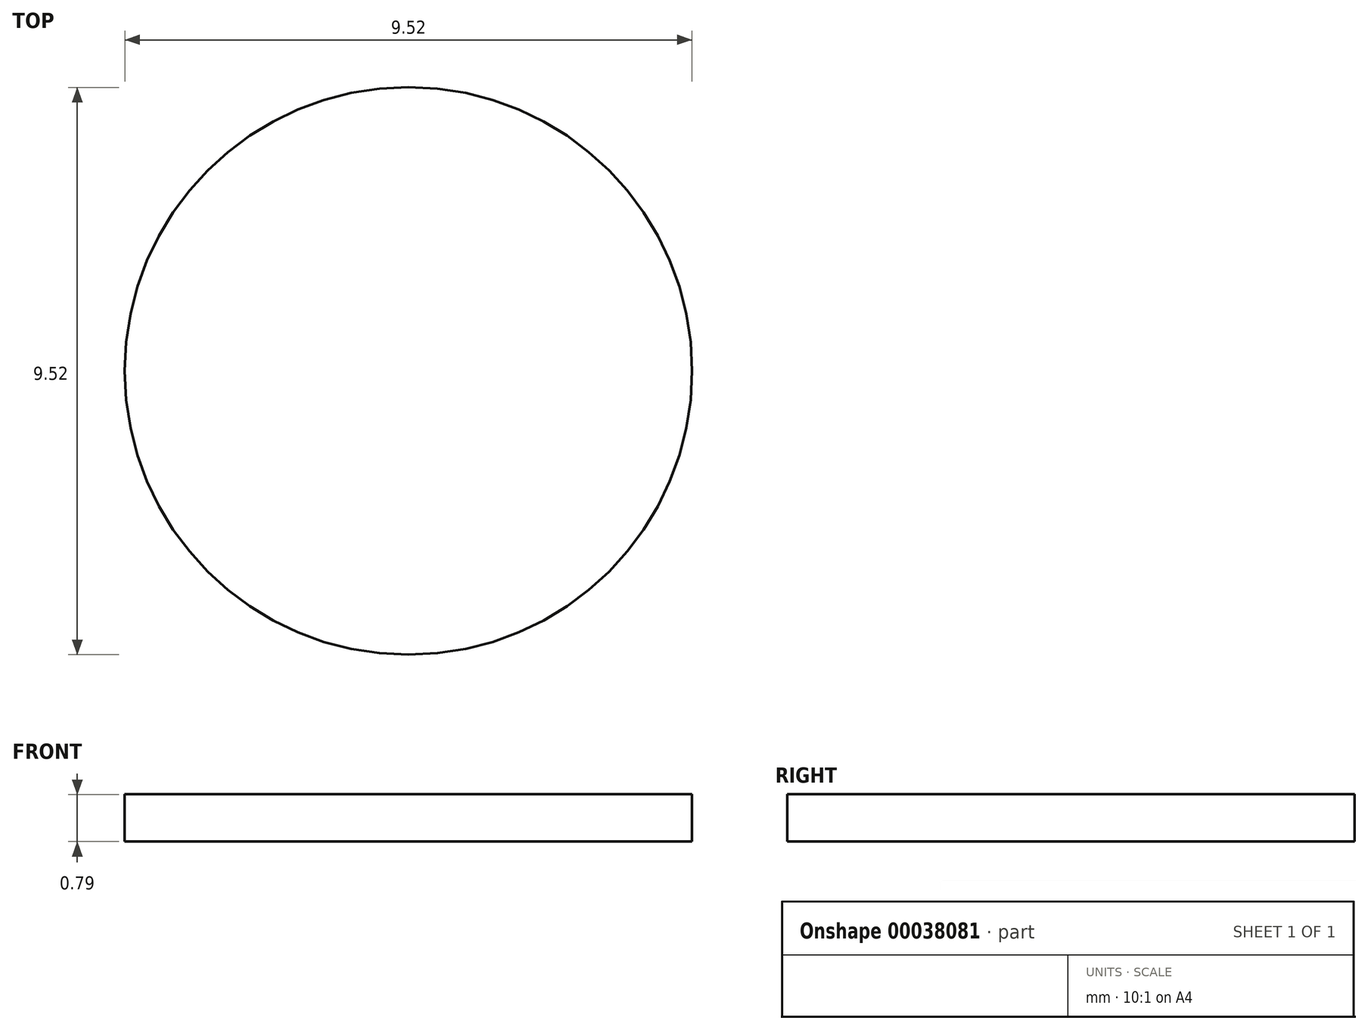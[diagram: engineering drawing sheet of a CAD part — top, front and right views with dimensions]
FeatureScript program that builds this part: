
annotation { "Feature Type Name" : "Feature", "Feature Type Description" : "" }
export const myFeature = defineFeature(function(context is Context, id is Id, definition is map)
    precondition{}
    {
        {
            var Q0;
            Q0=qCreatedBy(makeId("Top.planeOp"),FACE);
            var sketch = newSketch(context, id + "F0", { "sketchPlane" : qUnion([Q0])});
            skCircle(sketch, "E0", {"center": v(0, 0) * mm, "radius": 4.76 * mm});
            skSolve(sketch);
        }
        {
            var Q0;
            Q0 = qSketchRegion(id + "F0", true);
            extrude(context, id + "F1", {"entities" : qUnion([Q0]), "depth" : 0.8 * mm});
        }
    });
